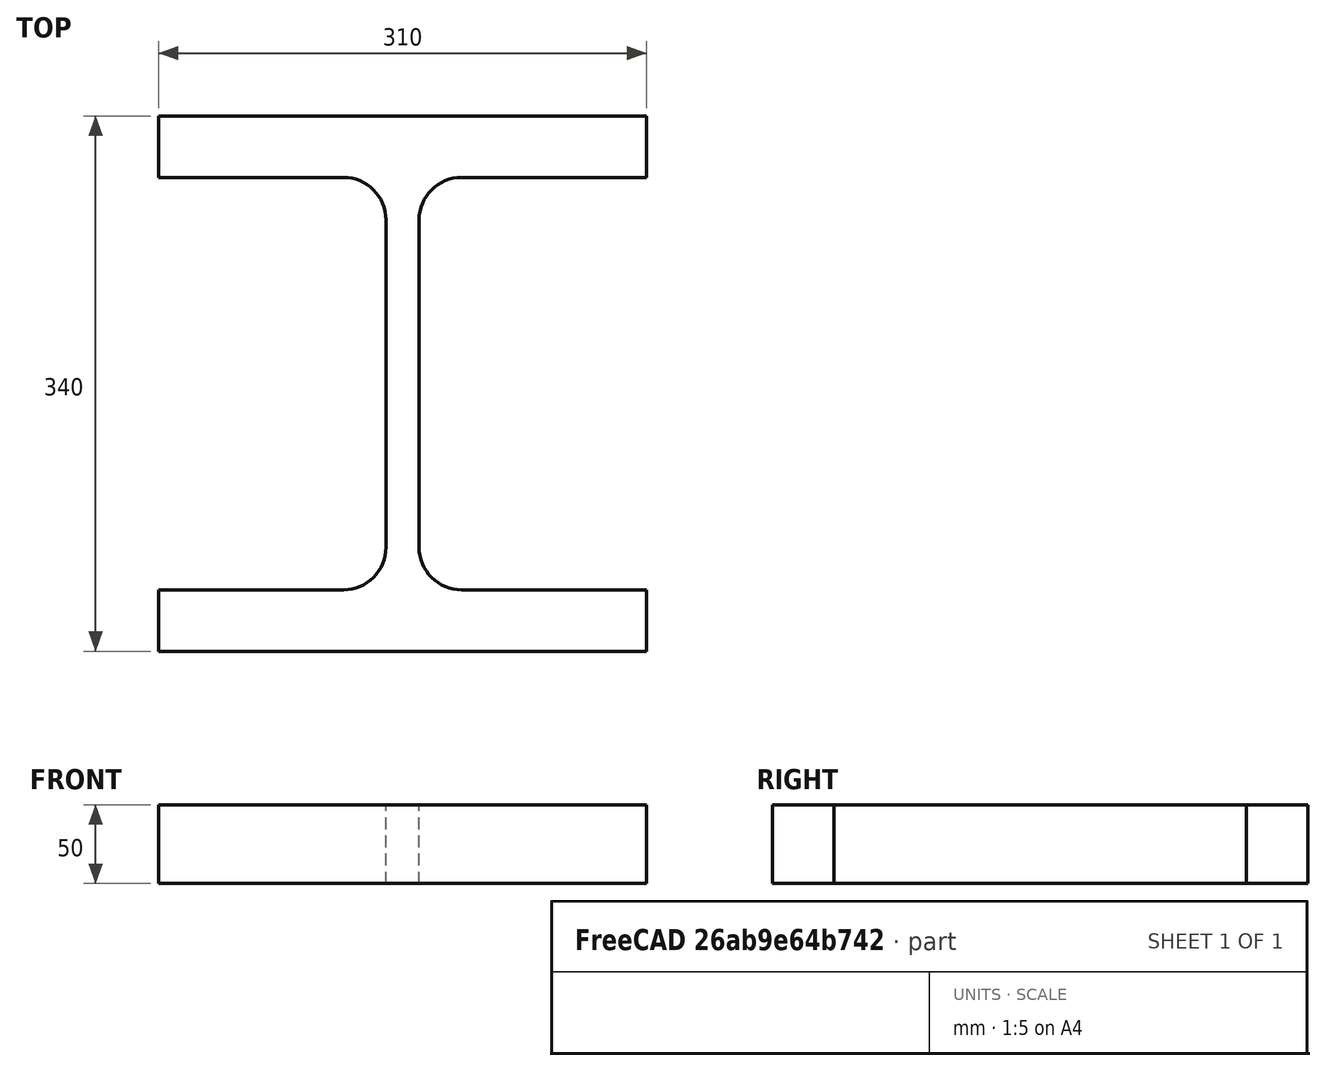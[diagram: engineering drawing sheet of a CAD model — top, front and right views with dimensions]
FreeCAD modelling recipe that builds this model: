
FCSTD DOCUMENT  (FreeCAD 0.15R4671 (Git))
Label: HE-M-Profile 300 DIN1025-4 S235JR
License: All rights reserved
LicenseURL: http://en.wikipedia.org/wiki/All_rights_reserved
objects: Sketcher::SketchObject×1, Part::Extrusion×1
note: 2 computed .brp shape members not serialized (recipe doc carries the construction recipe); baked Part::Feature solids carry a one-line shape summary decoded from their .brp

FEATURE [Sketcher::SketchObject] Sketch
  sketch-geometry (16):
    g0: LineSegment StartX=10.5 StartY=-104 StartZ=0 EndX=10.5 EndY=104 EndZ=0
    g1: LineSegment StartX=37.5 StartY=131 StartZ=0 EndX=155 EndY=131 EndZ=0
    g2: LineSegment StartX=155 StartY=131 StartZ=0 EndX=155 EndY=170 EndZ=0
    g3: LineSegment StartX=155 StartY=170 StartZ=0 EndX=-155 EndY=170 EndZ=0
    g4: LineSegment StartX=-155 StartY=170 StartZ=0 EndX=-155 EndY=131 EndZ=0
    g5: LineSegment StartX=-155 StartY=131 StartZ=0 EndX=-37.5 EndY=131 EndZ=0
    g6: LineSegment StartX=-10.5 StartY=104 StartZ=0 EndX=-10.5 EndY=-104 EndZ=0
    g7: LineSegment StartX=-37.5 StartY=-131 StartZ=0 EndX=-155 EndY=-131 EndZ=0
    g8: LineSegment StartX=-155 StartY=-131 StartZ=0 EndX=-155 EndY=-170 EndZ=0
    g9: LineSegment StartX=-155 StartY=-170 StartZ=0 EndX=155 EndY=-170 EndZ=0
    g10: LineSegment StartX=155 StartY=-170 StartZ=0 EndX=155 EndY=-131 EndZ=0
    g11: LineSegment StartX=155 StartY=-131 StartZ=0 EndX=37.5 EndY=-131 EndZ=0
    g12: ArcOfCircle CenterX=37.5 CenterY=104 CenterZ=0 NormalX=0 NormalY=0 NormalZ=1 Radius=27 StartAngle=1.5708 EndAngle=3.14159
    g13: ArcOfCircle CenterX=37.5 CenterY=-104 CenterZ=0 NormalX=0 NormalY=0 NormalZ=1 Radius=27 StartAngle=3.14159 EndAngle=4.71239
    g14: ArcOfCircle CenterX=-37.5 CenterY=104 CenterZ=0 NormalX=0 NormalY=0 NormalZ=1 Radius=27 StartAngle=0 EndAngle=1.5708
    g15: ArcOfCircle CenterX=-37.5 CenterY=-104 CenterZ=0 NormalX=0 NormalY=0 NormalZ=1 Radius=27 StartAngle=4.71239 EndAngle=6.28319
  constraints (42):
    c: Vertical(g0)
    c: Coincident(g2,g1)
    c: Vertical(g2)
    c: Coincident(g3,g2)
    c: Coincident(g4,g3)
    c: Vertical(g4)
    c: Coincident(g5,g4)
    c: Horizontal(g5)
    c: Vertical(g6)
    c: Horizontal(g7)
    c: Coincident(g8,g7)
    c: Vertical(g8)
    c: Coincident(g9,g8)
    c: Horizontal(g9)
    c: Coincident(g10,g9)
    c: Vertical(g10)
    c: Coincident(g11,g10)
    c: Horizontal(g11)
    c: Tangent(g1,g12) = 1.5708
    c: Tangent(g0,g12) = 1.5708
    c: Tangent(g0,g13) = 1.5708
    c: Tangent(g11,g13) = 1.5708
    c: Tangent(g5,g14) = 1.5708
    c: Tangent(g6,g14) = 1.5708
    c: Tangent(g6,g15) = 1.5708
    c: Tangent(g7,g15) = 1.5708
    c: Equal(g3,g9)
    c: Equal(g2,g4)
    c: Equal(g4,g8)
    c: Equal(g8,g10)
    c: Equal(g12,g14)
    c: Equal(g14,g15)
    c: Equal(g15,g13)
    c: Symmetric(g2,g3,g-2)
    c: Symmetric(g9,g8,g-2)
    c: Symmetric(g0,g6,g-2)
    c: Symmetric(g2,g9,g-1)
    c: DistanceY(g2,g9) = -340
    c: DistanceX(g3) = -310
    c: DistanceX(g0,g6) = -21
    c: DistanceY(g2) = 39
    c: Radius(g12) = 27
FEATURE [Part::Extrusion] Extrude  label="HE-M-Profile 300 DIN1025-4 S235JR"
  Base = -> Sketch
  Dir = (0,0,50)
  Solid = true
